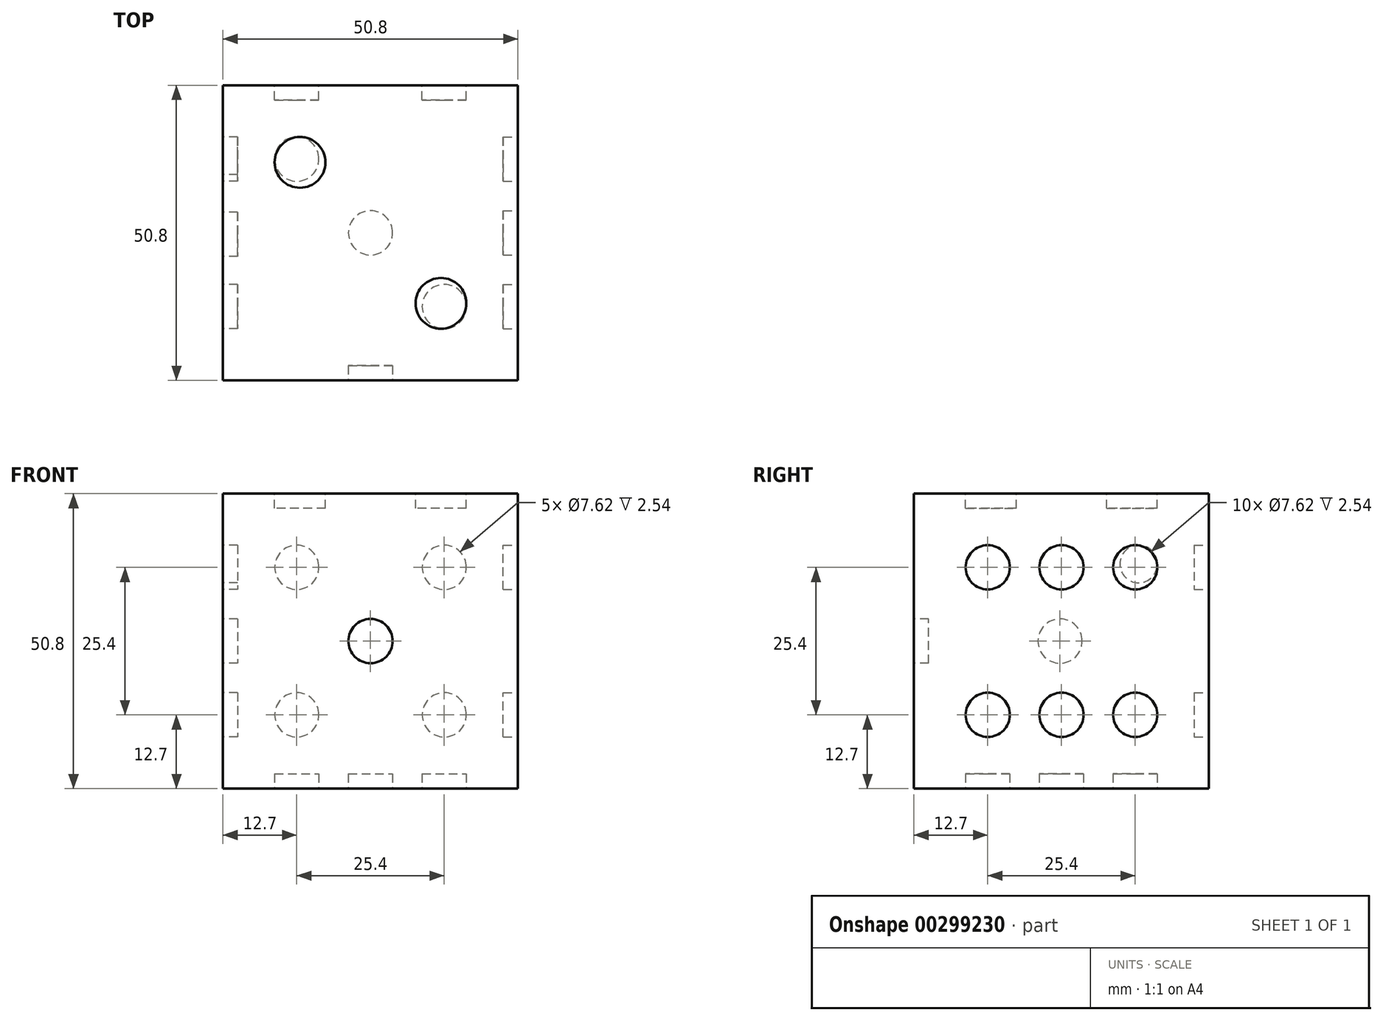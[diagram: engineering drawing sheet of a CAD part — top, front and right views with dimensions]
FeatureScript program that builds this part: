
annotation { "Feature Type Name" : "Feature", "Feature Type Description" : "" }
export const myFeature = defineFeature(function(context is Context, id is Id, definition is map)
    precondition{}
    {
        {
            var Q0;
            Q0=qCreatedBy(makeId("Front.planeOp"),FACE);
            var sketch = newSketch(context, id + "F0", { "sketchPlane" : qUnion([Q0])});
            skLineSegment(sketch, "E0", {"start": v(0, 0) * mm, "end": v(0, -50.8) * mm});
            skLineSegment(sketch, "E1", {"start": v(0, -50.8) * mm, "end": v(50.8, -50.8) * mm});
            skLineSegment(sketch, "E2", {"start": v(50.8, -50.8) * mm, "end": v(50.8, 0) * mm});
            skLineSegment(sketch, "E3", {"start": v(50.8, 0) * mm, "end": v(0, 0) * mm});
            skSolve(sketch);
        }
        {
            var Q0;
            Q0=makeQuery(id+"F0.imprint","IMPRINT",FACE,{"disambiguationData":[TD([[makeQuery(id+"F0.imprint","IMPRINT",EDGE,{"derivedFrom":sQuery(id+"F0.wireOp",EDGE,"E0")}),1.0]])]});
            extrude(context, id + "F1", {"entities" : qUnion([Q0]), "depth" : 50.8 * mm});
        }
        {
            var Q0;
            Q0=makeQuery(id+"F1.opExtrude","SWEPT_FACE",FACE,{"disambiguationData":[OSD([sQuery(id+"F0.wireOp",EDGE,"E1")])]});
            var sketch = newSketch(context, id + "F2", { "sketchPlane" : qUnion([Q0])});
            skCircle(sketch, "E4", {"center": v(25.4, 25.4) * mm, "radius": 3.81 * mm});
            skSolve(sketch);
        }
        {
            var Q0;
            Q0=makeQuery(id+"F1.opExtrude","SWEPT_FACE",FACE,{"disambiguationData":[OSD([sQuery(id+"F0.wireOp",EDGE,"E3")])]});
            var sketch = newSketch(context, id + "F3", { "sketchPlane" : qUnion([Q0])});
            skSolve(sketch);
        }
        {
            var Q0;
            Q0=makeQuery(id+"F2.imprint","IMPRINT",FACE,{"disambiguationData":[TD([[makeQuery(id+"F2.imprint","IMPRINT",EDGE,{"derivedFrom":sQuery(id+"F2.wireOp",EDGE,"E4")}),-1.0]])]});
            var sketch = newSketch(context, id + "F4", { "sketchPlane" : qUnion([Q0])});
            skSolve(sketch);
        }
        {
            var Q0;
            Q0=makeQuery(id+"F4.imprint","IMPRINT",FACE,{"disambiguationData":[TD([[makeQuery(id+"F4.imprint","IMPRINT",EDGE,{"derivedFrom":makeQuery(id+"F2.imprint","IMPRINT",EDGE,{"derivedFrom":sQuery(id+"F2.wireOp",EDGE,"E4")})}),-1.0]])]});
            var sketch = newSketch(context, id + "F5", { "sketchPlane" : qUnion([Q0])});
            skSolve(sketch);
        }
        {
            var Q0;
            Q0=makeQuery(id+"F1.opExtrude","CAP_FACE",FACE,{"disambiguationData":[OSD([sQuery(id+"F0.wireOp",EDGE,"E0"),sQuery(id+"F0.wireOp",EDGE,"E1"),sQuery(id+"F0.wireOp",EDGE,"E2"),sQuery(id+"F0.wireOp",EDGE,"E3")])],"isStart":false});
            var sketch = newSketch(context, id + "F6", { "sketchPlane" : qUnion([Q0])});
            skCircle(sketch, "E5", {"center": v(25.4, -25.4) * mm, "radius": 3.81 * mm});
            skSolve(sketch);
        }
        {
            var Q0;
            Q0=makeQuery(id+"F6.imprint","IMPRINT",FACE,{"disambiguationData":[TD([[makeQuery(id+"F6.imprint","IMPRINT",EDGE,{"derivedFrom":sQuery(id+"F6.wireOp",EDGE,"E5")}),-1.0]])]});
            var sketch = newSketch(context, id + "F7", { "sketchPlane" : qUnion([Q0])});
            skSolve(sketch);
        }
        {
            var Q0;
            {var subQ0=sQuery(id+"F0.wireOp",EDGE,"E3");Q0=makeQuery(id+"F3.imprint","IMPRINT",FACE,{"disambiguationData":[TD([[makeQuery(id+"F3.imprint","IMPRINT",EDGE,{"derivedFrom":makeQuery(id+"F1.opExtrude","CAP_EDGE",EDGE,{"disambiguationData":[OSD([subQ0])],"isStart":true})}),1.0]])]});}
            var sketch = newSketch(context, id + "F8", { "sketchPlane" : qUnion([Q0])});
            skCircle(sketch, "E6", {"center": v(13.27, -13.27) * mm, "radius": 4.38 * mm});
            skCircle(sketch, "E7", {"center": v(37.53, -37.53) * mm, "radius": 4.38 * mm});
            skSolve(sketch);
        }
        {
            var Q0;
            Q0=makeQuery(id+"F5.imprint","IMPRINT",FACE,{"disambiguationData":[TD([[makeQuery(id+"F5.imprint","IMPRINT",EDGE,{"derivedFrom":makeQuery(id+"F4.imprint","IMPRINT",EDGE,{"derivedFrom":makeQuery(id+"F2.imprint","IMPRINT",EDGE,{"derivedFrom":sQuery(id+"F2.wireOp",EDGE,"E4")})})}),-1.0]])]});
            var sketch = newSketch(context, id + "F9", { "sketchPlane" : qUnion([Q0])});
            skCircle(sketch, "E8", {"center": v(38.1, 38.1) * mm, "radius": 3.81 * mm});
            skCircle(sketch, "E9", {"center": v(12.7, 12.7) * mm, "radius": 3.81 * mm});
            skSolve(sketch);
        }
        {
            var Q0;
            Q0=makeQuery(id+"F1.opExtrude","CAP_FACE",FACE,{"disambiguationData":[OSD([sQuery(id+"F0.wireOp",EDGE,"E0"),sQuery(id+"F0.wireOp",EDGE,"E1"),sQuery(id+"F0.wireOp",EDGE,"E2"),sQuery(id+"F0.wireOp",EDGE,"E3")])],"isStart":true});
            var sketch = newSketch(context, id + "F10", { "sketchPlane" : qUnion([Q0])});
            skCircle(sketch, "E10", {"center": v(-38.1, -38.1) * mm, "radius": 3.81 * mm});
            skCircle(sketch, "E11", {"center": v(-12.7, -12.7) * mm, "radius": 3.81 * mm});
            skCircle(sketch, "E12", {"center": v(-38.1, -12.7) * mm, "radius": 3.81 * mm});
            skCircle(sketch, "E13", {"center": v(-12.7, -38.1) * mm, "radius": 3.81 * mm});
            skSolve(sketch);
        }
        {
            var Q0;
            Q0=makeQuery(id+"F1.opExtrude","SWEPT_FACE",FACE,{"disambiguationData":[OSD([sQuery(id+"F0.wireOp",EDGE,"E0")])]});
            var sketch = newSketch(context, id + "F11", { "sketchPlane" : qUnion([Q0])});
            skCircle(sketch, "E14", {"center": v(12.12, -12.12) * mm, "radius": 3.23 * mm});
            skCircle(sketch, "E15", {"center": v(12.7, -38.1) * mm, "radius": 3.81 * mm});
            skCircle(sketch, "E16", {"center": v(38.1, -12.7) * mm, "radius": 3.81 * mm});
            skCircle(sketch, "E17", {"center": v(38.1, -38.1) * mm, "radius": 3.81 * mm});
            skCircle(sketch, "E18", {"center": v(25.66, -25.4) * mm, "radius": 3.81 * mm});
            skSolve(sketch);
        }
        {
            var Q0;
            Q0=makeQuery(id+"F1.opExtrude","SWEPT_FACE",FACE,{"disambiguationData":[OSD([sQuery(id+"F0.wireOp",EDGE,"E2")])]});
            var sketch = newSketch(context, id + "F12", { "sketchPlane" : qUnion([Q0])});
            skCircle(sketch, "E19", {"center": v(-38.1, -38.1) * mm, "radius": 3.8 * mm});
            skCircle(sketch, "E20", {"center": v(-12.7, -12.7) * mm, "radius": 3.81 * mm});
            skCircle(sketch, "E21", {"center": v(-25.4, -12.7) * mm, "radius": 3.81 * mm});
            skCircle(sketch, "E22", {"center": v(-38.1, -12.7) * mm, "radius": 3.81 * mm});
            skCircle(sketch, "E23", {"center": v(-12.7, -38.1) * mm, "radius": 3.81 * mm});
            skCircle(sketch, "E24", {"center": v(-25.4, -38.1) * mm, "radius": 3.81 * mm});
            skSolve(sketch);
        }
        {
            var Q0;
            Q0=makeQuery(id+"F7.imprint","IMPRINT",FACE,{"disambiguationData":[TD([[makeQuery(id+"F7.imprint","IMPRINT",EDGE,{"derivedFrom":makeQuery(id+"F6.imprint","IMPRINT",EDGE,{"derivedFrom":sQuery(id+"F6.wireOp",EDGE,"E5")})}),1.0]])]});
            var Q1;
            Q1=sQuery(id+"F6.wireOp",EDGE,"E5");
            extrude(context, id + "F13", {"entities" : qUnion([Q0]), "operationType" : NewBodyOperationType.REMOVE, "surfaceEntities" : qUnion([Q1]), "oppositeDirection" : true, "depth" : 2.54 * mm});
        }
        {
            var Q0;
            Q0=makeQuery(id+"F8.imprint","IMPRINT",FACE,{"disambiguationData":[TD([[makeQuery(id+"F8.imprint","IMPRINT",EDGE,{"derivedFrom":sQuery(id+"F8.wireOp",EDGE,"E6")}),1.0]])]});
            var Q1;
            Q1=makeQuery(id+"F8.imprint","IMPRINT",FACE,{"disambiguationData":[TD([[makeQuery(id+"F8.imprint","IMPRINT",EDGE,{"derivedFrom":sQuery(id+"F8.wireOp",EDGE,"E7")}),1.0]])]});
            var Q2;
            Q2=sQuery(id+"F8.wireOp",EDGE,"E7");
            var Q3;
            Q3=sQuery(id+"F8.wireOp",EDGE,"E6");
            extrude(context, id + "F14", {"entities" : qUnion([Q0, Q1]), "operationType" : NewBodyOperationType.REMOVE, "surfaceEntities" : qUnion([Q2, Q3]), "oppositeDirection" : true, "depth" : 2.54 * mm});
        }
        {
            var Q0;
            Q0=makeQuery(id+"F12.imprint","IMPRINT",FACE,{"disambiguationData":[TD([[makeQuery(id+"F12.imprint","IMPRINT",EDGE,{"derivedFrom":sQuery(id+"F12.wireOp",EDGE,"E23")}),1.0]])]});
            var Q1;
            Q1=makeQuery(id+"F12.imprint","IMPRINT",FACE,{"disambiguationData":[TD([[makeQuery(id+"F12.imprint","IMPRINT",EDGE,{"derivedFrom":sQuery(id+"F12.wireOp",EDGE,"E24")}),1.0]])]});
            var Q2;
            Q2=makeQuery(id+"F12.imprint","IMPRINT",FACE,{"disambiguationData":[TD([[makeQuery(id+"F12.imprint","IMPRINT",EDGE,{"derivedFrom":sQuery(id+"F12.wireOp",EDGE,"E19")}),1.0]])]});
            var Q3;
            Q3=makeQuery(id+"F12.imprint","IMPRINT",FACE,{"disambiguationData":[TD([[makeQuery(id+"F12.imprint","IMPRINT",EDGE,{"derivedFrom":sQuery(id+"F12.wireOp",EDGE,"E22")}),1.0]])]});
            var Q4;
            Q4=makeQuery(id+"F12.imprint","IMPRINT",FACE,{"disambiguationData":[TD([[makeQuery(id+"F12.imprint","IMPRINT",EDGE,{"derivedFrom":sQuery(id+"F12.wireOp",EDGE,"E20")}),1.0]])]});
            var Q5;
            Q5=makeQuery(id+"F12.imprint","IMPRINT",FACE,{"disambiguationData":[TD([[makeQuery(id+"F12.imprint","IMPRINT",EDGE,{"derivedFrom":sQuery(id+"F12.wireOp",EDGE,"E21")}),1.0]])]});
            extrude(context, id + "F15", {"entities" : qUnion([Q0, Q1, Q2, Q3, Q4, Q5]), "operationType" : NewBodyOperationType.REMOVE, "oppositeDirection" : true, "depth" : 2.54 * mm});
        }
        {
            var Q0;
            Q0=makeQuery(id+"F10.imprint","IMPRINT",FACE,{"disambiguationData":[TD([[makeQuery(id+"F10.imprint","IMPRINT",EDGE,{"derivedFrom":sQuery(id+"F10.wireOp",EDGE,"E11")}),1.0]])]});
            var Q1;
            Q1=makeQuery(id+"F10.imprint","IMPRINT",FACE,{"disambiguationData":[TD([[makeQuery(id+"F10.imprint","IMPRINT",EDGE,{"derivedFrom":sQuery(id+"F10.wireOp",EDGE,"E13")}),1.0]])]});
            var Q2;
            Q2=makeQuery(id+"F10.imprint","IMPRINT",FACE,{"disambiguationData":[TD([[makeQuery(id+"F10.imprint","IMPRINT",EDGE,{"derivedFrom":sQuery(id+"F10.wireOp",EDGE,"E10")}),1.0]])]});
            var Q3;
            Q3=makeQuery(id+"F10.imprint","IMPRINT",FACE,{"disambiguationData":[TD([[makeQuery(id+"F10.imprint","IMPRINT",EDGE,{"derivedFrom":sQuery(id+"F10.wireOp",EDGE,"E12")}),1.0]])]});
            extrude(context, id + "F16", {"entities" : qUnion([Q0, Q1, Q2, Q3]), "operationType" : NewBodyOperationType.REMOVE, "oppositeDirection" : true, "depth" : 2.54 * mm});
        }
        {
            var Q0;
            Q0=makeQuery(id+"F11.imprint","IMPRINT",FACE,{"disambiguationData":[TD([[makeQuery(id+"F11.imprint","IMPRINT",EDGE,{"derivedFrom":sQuery(id+"F11.wireOp",EDGE,"E17")}),1.0]])]});
            var Q1;
            Q1=makeQuery(id+"F11.imprint","IMPRINT",FACE,{"disambiguationData":[TD([[makeQuery(id+"F11.imprint","IMPRINT",EDGE,{"derivedFrom":sQuery(id+"F11.wireOp",EDGE,"E18")}),1.0]])]});
            var Q2;
            Q2=makeQuery(id+"F11.imprint","IMPRINT",FACE,{"disambiguationData":[TD([[makeQuery(id+"F11.imprint","IMPRINT",EDGE,{"derivedFrom":sQuery(id+"F11.wireOp",EDGE,"E14")}),1.0]])]});
            var Q3;
            Q3=makeQuery(id+"F11.imprint","IMPRINT",FACE,{"disambiguationData":[TD([[makeQuery(id+"F11.imprint","IMPRINT",EDGE,{"derivedFrom":sQuery(id+"F11.wireOp",EDGE,"E16")}),1.0]])]});
            var Q4;
            Q4=makeQuery(id+"F11.imprint","IMPRINT",FACE,{"disambiguationData":[TD([[makeQuery(id+"F11.imprint","IMPRINT",EDGE,{"derivedFrom":sQuery(id+"F11.wireOp",EDGE,"E15")}),1.0]])]});
            extrude(context, id + "F17", {"entities" : qUnion([Q0, Q1, Q2, Q3, Q4]), "operationType" : NewBodyOperationType.REMOVE, "oppositeDirection" : true, "depth" : 2.54 * mm});
        }
        {
            var Q0;
            Q0=makeQuery(id+"F5.imprint","IMPRINT",FACE,{"disambiguationData":[TD([[makeQuery(id+"F5.imprint","IMPRINT",EDGE,{"derivedFrom":makeQuery(id+"F4.imprint","IMPRINT",EDGE,{"derivedFrom":makeQuery(id+"F2.imprint","IMPRINT",EDGE,{"derivedFrom":sQuery(id+"F2.wireOp",EDGE,"E4")})})}),1.0]])]});
            var Q1;
            Q1=makeQuery(id+"F9.imprint","IMPRINT",FACE,{"disambiguationData":[TD([[makeQuery(id+"F9.imprint","IMPRINT",EDGE,{"derivedFrom":sQuery(id+"F9.wireOp",EDGE,"E8")}),1.0]])]});
            var Q2;
            Q2=makeQuery(id+"F9.imprint","IMPRINT",FACE,{"disambiguationData":[TD([[makeQuery(id+"F9.imprint","IMPRINT",EDGE,{"derivedFrom":sQuery(id+"F9.wireOp",EDGE,"E9")}),1.0]])]});
            var Q3;
            Q3=sQuery(id+"F9.wireOp",EDGE,"E8");
            var Q4;
            Q4=sQuery(id+"F2.wireOp",EDGE,"E4");
            var Q5;
            Q5=sQuery(id+"F9.wireOp",EDGE,"E9");
            extrude(context, id + "F18", {"entities" : qUnion([Q0, Q1, Q2]), "operationType" : NewBodyOperationType.REMOVE, "surfaceEntities" : qUnion([Q3, Q4, Q5]), "oppositeDirection" : true, "depth" : 2.54 * mm});
        }
    });
